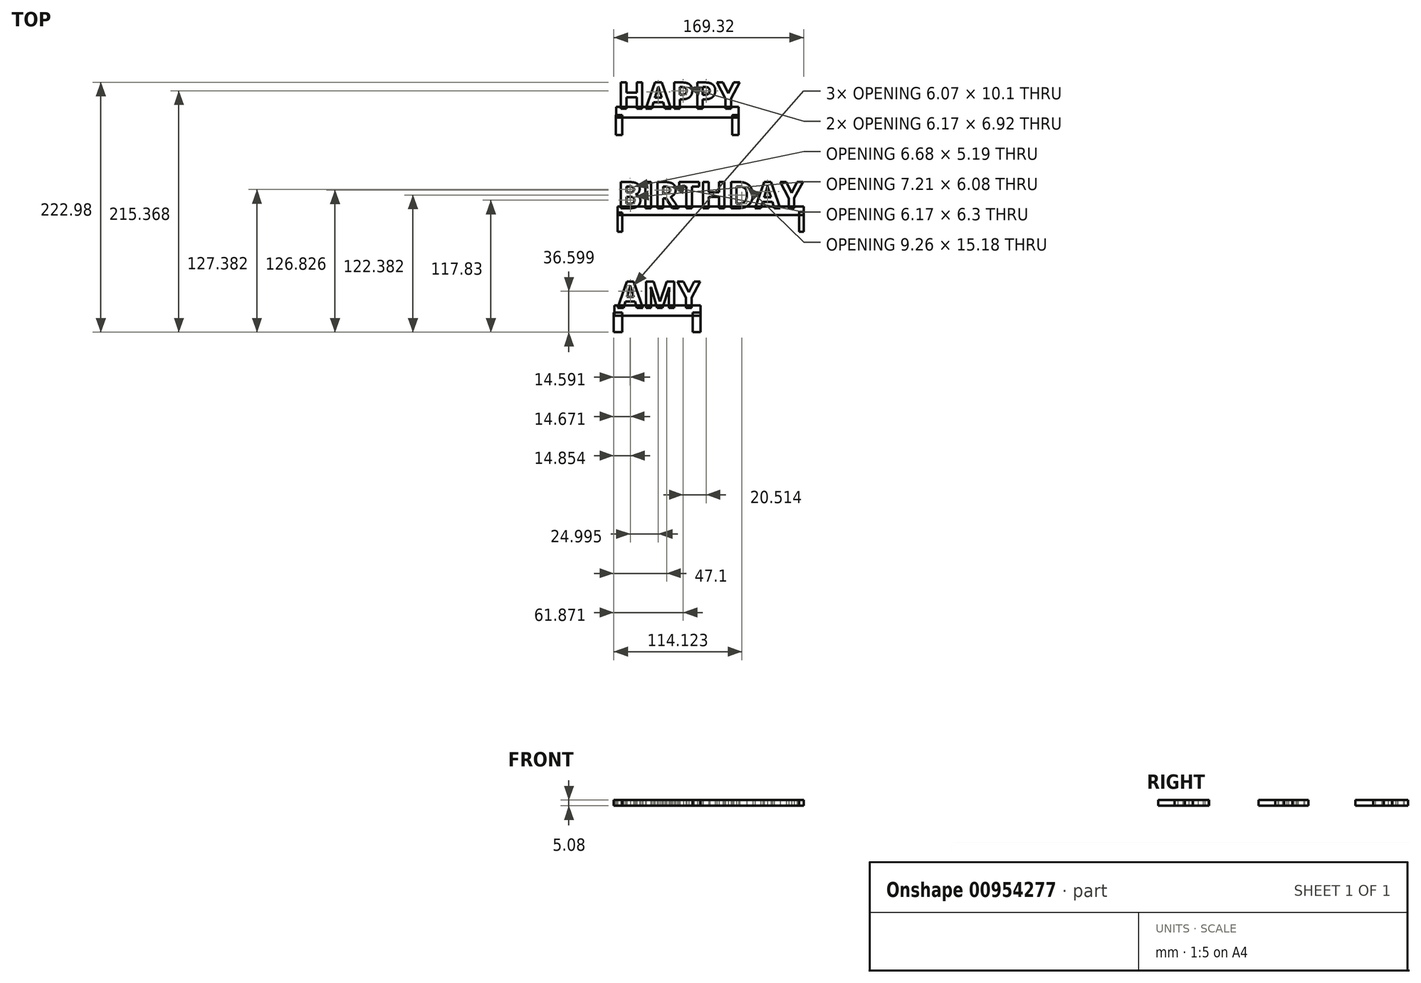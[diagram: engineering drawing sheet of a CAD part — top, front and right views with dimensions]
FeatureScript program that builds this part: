
annotation { "Feature Type Name" : "Feature", "Feature Type Description" : "" }
export const myFeature = defineFeature(function(context is Context, id is Id, definition is map)
    precondition{}
    {
        {
            var Q0;
            Q0=qCreatedBy(makeId("Top.planeOp"),FACE);
            var sketch = newSketch(context, id + "F0", { "sketchPlane" : qUnion([Q0])});
            skText(sketch, "E0", { "text": "HAPPY\n\nBIRTHDAY\n\nAMY", "fontName": "OpenSans-Bold.ttf"});
            const initialGuessF0  = {"E0": [-0.08215, 0.08137, 1, 0, 0.02352]};
            skSetInitialGuess(sketch, initialGuessF0);
            skSolve(sketch);
        }
        {
            var Q0;
            Q0 = qSketchRegion(id + "F0", true);
            extrude(context, id + "F1", {"entities" : qUnion([Q0]), "depth" : 5.08 * mm, "offsetDistance" : 25.4 * mm});
        }
        {
            var Q0;
            Q0=qCreatedBy(makeId("Top.planeOp"),FACE);
            var sketch = newSketch(context, id + "F2", { "sketchPlane" : qUnion([Q0])});
            skLineSegment(sketch, "E1.bottom", {"start": v(-83.55, 83.04) * mm, "end": v(25.86, 83.04) * mm});
            skLineSegment(sketch, "E1.top", {"start": v(-83.55, 73.45) * mm, "end": v(25.86, 73.45) * mm});
            skLineSegment(sketch, "E1.left", {"start": v(-83.55, 83.04) * mm, "end": v(-83.55, 73.45) * mm});
            skLineSegment(sketch, "E1.right", {"start": v(25.86, 83.04) * mm, "end": v(25.86, 73.45) * mm});
            skSolve(sketch);
        }
        {
            var Q0;
            Q0 = qSketchRegion(id + "F2", true);
            extrude(context, id + "F3", {"entities" : qUnion([Q0]), "depth" : 5.08 * mm, "offsetDistance" : 25.4 * mm});
        }
        {
            var Q0;
            Q0=qCreatedBy(makeId("Top.planeOp"),FACE);
            var sketch = newSketch(context, id + "F4", { "sketchPlane" : qUnion([Q0])});
            skLineSegment(sketch, "E2.bottom", {"start": v(-82.08, -13.62) * mm, "end": v(83.8, -13.62) * mm});
            skLineSegment(sketch, "E2.top", {"start": v(-82.08, -5.86) * mm, "end": v(83.8, -5.86) * mm});
            skLineSegment(sketch, "E2.left", {"start": v(-82.08, -13.62) * mm, "end": v(-82.08, -5.86) * mm});
            skLineSegment(sketch, "E2.right", {"start": v(83.8, -13.62) * mm, "end": v(83.8, -5.86) * mm});
            skSolve(sketch);
        }
        {
            var Q0;
            Q0 = qSketchRegion(id + "F4", true);
            extrude(context, id + "F5", {"entities" : qUnion([Q0]), "depth" : 5.08 * mm, "offsetDistance" : 25.4 * mm});
        }
        {
            var Q0;
            Q0=qCreatedBy(makeId("Top.planeOp"),FACE);
            var sketch = newSketch(context, id + "F6", { "sketchPlane" : qUnion([Q0])});
            skLineSegment(sketch, "E3.bottom", {"start": v(-85, -94.27) * mm, "end": v(-8.15, -94.27) * mm});
            skLineSegment(sketch, "E3.top", {"start": v(-85, -103.54) * mm, "end": v(-8.15, -103.54) * mm});
            skLineSegment(sketch, "E3.left", {"start": v(-85, -94.27) * mm, "end": v(-85, -103.54) * mm});
            skLineSegment(sketch, "E3.right", {"start": v(-8.15, -94.27) * mm, "end": v(-8.15, -103.54) * mm});
            skSolve(sketch);
        }
        {
            var Q0;
            Q0 = qSketchRegion(id + "F6", true);
            extrude(context, id + "F7", {"entities" : qUnion([Q0]), "depth" : 5.08 * mm, "offsetDistance" : 25.4 * mm});
        }
        {
            var Q0;
            Q0=qCreatedBy(makeId("Top.planeOp"),FACE);
            var sketch = newSketch(context, id + "F8", { "sketchPlane" : qUnion([Q0])});
            skLineSegment(sketch, "E4.bottom", {"start": v(-83.76, 75.58) * mm, "end": v(-78.06, 75.58) * mm});
            skLineSegment(sketch, "E4.top", {"start": v(-83.76, 57.82) * mm, "end": v(-78.06, 57.82) * mm});
            skLineSegment(sketch, "E4.left", {"start": v(-83.76, 75.58) * mm, "end": v(-83.76, 57.82) * mm});
            skLineSegment(sketch, "E4.right", {"start": v(-78.06, 75.58) * mm, "end": v(-78.06, 57.82) * mm});
            skLineSegment(sketch, "E5.bottom", {"start": v(25.78, 75.58) * mm, "end": v(20.08, 75.58) * mm});
            skLineSegment(sketch, "E5.top", {"start": v(25.78, 57.82) * mm, "end": v(20.08, 57.82) * mm});
            skLineSegment(sketch, "E5.left", {"start": v(25.78, 75.58) * mm, "end": v(25.78, 57.82) * mm});
            skLineSegment(sketch, "E5.right", {"start": v(20.08, 75.58) * mm, "end": v(20.08, 57.82) * mm});
            skLineSegment(sketch, "E6.bottom", {"start": v(-82.08, -11.52) * mm, "end": v(-78.06, -11.52) * mm});
            skLineSegment(sketch, "E6.top", {"start": v(-82.08, -28.6) * mm, "end": v(-78.06, -28.6) * mm});
            skLineSegment(sketch, "E6.left", {"start": v(-82.08, -11.52) * mm, "end": v(-82.08, -28.6) * mm});
            skLineSegment(sketch, "E6.right", {"start": v(-78.06, -11.52) * mm, "end": v(-78.06, -28.6) * mm});
            skLineSegment(sketch, "E7.bottom", {"start": v(83.73, -10.85) * mm, "end": v(79.71, -10.85) * mm});
            skLineSegment(sketch, "E7.top", {"start": v(83.73, -28.6) * mm, "end": v(79.71, -28.6) * mm});
            skLineSegment(sketch, "E7.left", {"start": v(83.73, -10.85) * mm, "end": v(83.73, -28.6) * mm});
            skLineSegment(sketch, "E7.right", {"start": v(79.71, -10.85) * mm, "end": v(79.71, -28.6) * mm});
            skLineSegment(sketch, "E8.bottom", {"start": v(-85.52, -100.75) * mm, "end": v(-78.06, -100.75) * mm});
            skLineSegment(sketch, "E8.top", {"start": v(-85.52, -118.19) * mm, "end": v(-78.06, -118.19) * mm});
            skLineSegment(sketch, "E8.left", {"start": v(-85.52, -100.75) * mm, "end": v(-85.52, -118.19) * mm});
            skLineSegment(sketch, "E8.right", {"start": v(-78.06, -100.75) * mm, "end": v(-78.06, -118.19) * mm});
            skLineSegment(sketch, "E9.bottom", {"start": v(-8.28, -100.75) * mm, "end": v(-15.26, -100.75) * mm});
            skLineSegment(sketch, "E9.top", {"start": v(-8.28, -118.19) * mm, "end": v(-15.26, -118.19) * mm});
            skLineSegment(sketch, "E9.left", {"start": v(-8.28, -100.75) * mm, "end": v(-8.28, -118.19) * mm});
            skLineSegment(sketch, "E9.right", {"start": v(-15.26, -100.75) * mm, "end": v(-15.26, -118.19) * mm});
            skSolve(sketch);
        }
        {
            var Q0;
            Q0 = qSketchRegion(id + "F8", true);
            extrude(context, id + "F9", {"entities" : qUnion([Q0]), "depth" : 5.08 * mm, "offsetDistance" : 25.4 * mm});
        }
    });
